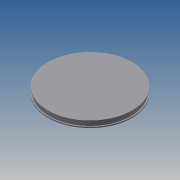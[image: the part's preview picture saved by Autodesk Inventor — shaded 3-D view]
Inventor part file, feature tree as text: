
AUTODESK INVENTOR PART (.ipt)
format: ipt  version: 2013 (Build 170138000, 138)  size: 127,488 bytes
history: native  units: mm
features: extrude x7, sketch x7
ambient origin geometry x8: Origin, YZ Plane, XZ Plane, XY Plane, X Axis, Y Axis, Z Axis, Center Point
bodies: Solid1 (feature_tree)
feature tree (14):
  extrude  "Extrusion1"  Depth=1.5mm TaperAngle=0.0deg
  extrude  "Extrusion2"  Depth=7.0mm TaperAngle=0.0deg
  extrude  "Extrusion3"  Depth=100.0mm
  extrude  "Extrusion5"  Depth=25.0mm
  extrude  "Extrusion6"  Depth=90.0mm
  extrude  "Extrusion7"  Depth=70.0mm
  extrude  "Extrusion8"  [1 undecoded]
  sketch  "Sketch1"  dims[d0=154.0mm d2=1.5mm d3=0.0mm]
  sketch  "Sketch2"  dims[d4=150.0mm d6=7.0mm d7=0.0mm]
  sketch  "Sketch3"  dims[d8=1.5mm d9=0.0mm d14=100.0mm]
  sketch  "Sketch5"  dims[d16=15.0mm d17=0.0mm d18=25.0mm]
  sketch  "Sketch6"  dims[d20=2.5mm d21=0.0mm d22=90.0mm]
  sketch  "Sketch7"  dims[d24=20.0mm d25=0.0mm d26=70.0mm]
  sketch  "Sketch8"  dims[d28=20.0mm d29=0.0mm]
note: 1 required parameter value undecoded (feature->parameter linkage not recoverable at this tier; creation-order binding heuristic only, values carry confidence <= 0.55)
